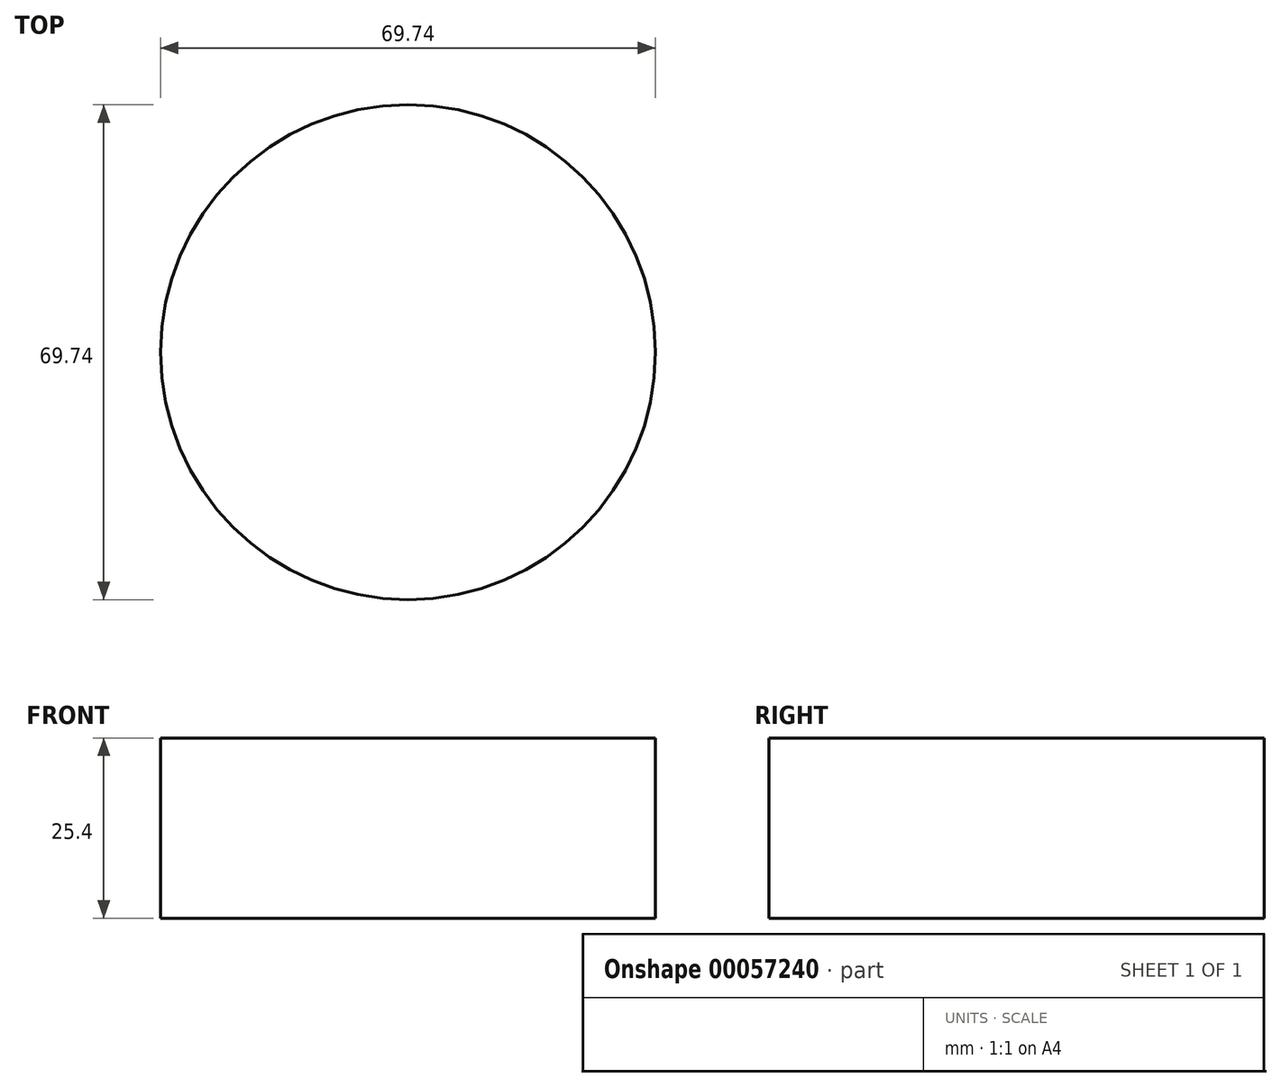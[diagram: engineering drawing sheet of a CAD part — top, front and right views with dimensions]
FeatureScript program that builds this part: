
annotation { "Feature Type Name" : "Feature", "Feature Type Description" : "" }
export const myFeature = defineFeature(function(context is Context, id is Id, definition is map)
    precondition{}
    {
        {
            var Q0;
            Q0=qCreatedBy(makeId("Top.planeOp"),FACE);
            var sketch = newSketch(context, id + "F0", { "sketchPlane" : qUnion([Q0])});
            skCircle(sketch, "E0", {"center": v(0, 0) * mm, "radius": 34.87 * mm});
            skSolve(sketch);
        }
        {
            var Q0;
            Q0 = qSketchRegion(id + "F0", true);
            extrude(context, id + "F1", {"entities" : qUnion([Q0]), "depth" : 25.4 * mm});
        }
    });
